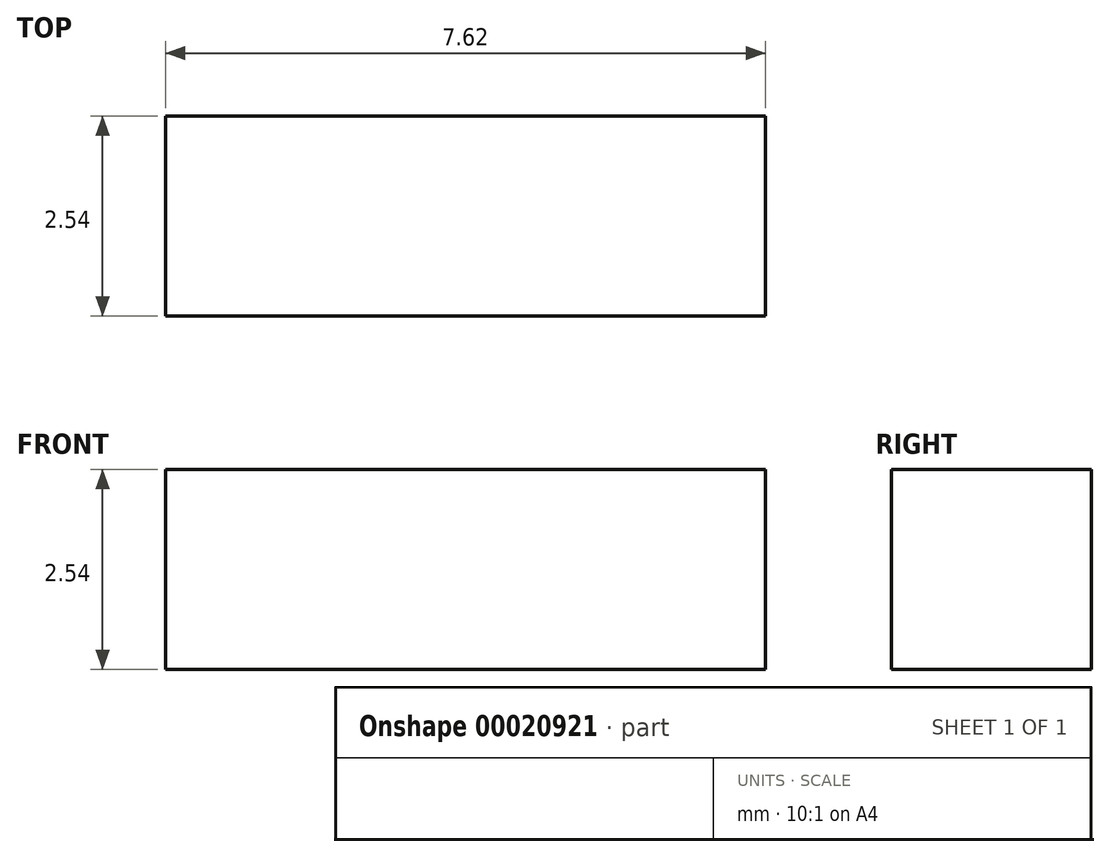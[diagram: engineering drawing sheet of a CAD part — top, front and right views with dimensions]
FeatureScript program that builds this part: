
annotation { "Feature Type Name" : "Feature", "Feature Type Description" : "" }
export const myFeature = defineFeature(function(context is Context, id is Id, definition is map)
    precondition{}
    {
        {
            var Q0;
            Q0=qCreatedBy(makeId("Front.planeOp"),FACE);
            var sketch = newSketch(context, id + "F0", { "sketchPlane" : qUnion([Q0])});
            skLineSegment(sketch, "E0.rect.bottom", {"start": v(3.81, 1.27) * mm, "end": v(-3.8, 1.27) * mm});
            skLineSegment(sketch, "E0.rect.top", {"start": v(3.81, -1.27) * mm, "end": v(-3.81, -1.27) * mm});
            skLineSegment(sketch, "E0.rect.left", {"start": v(3.81, 1.27) * mm, "end": v(3.81, -1.27) * mm});
            skLineSegment(sketch, "E0.rect.right", {"start": v(-3.81, 1.27) * mm, "end": v(-3.81, -1.27) * mm});
            skPoint(sketch, "E0.rect.middle", {"position": v(0, 0) * mm});
            skSolve(sketch);
        }
        {
            var Q0;
            Q0 = qSketchRegion(id + "F0", true);
            extrude(context, id + "F1", {"entities" : qUnion([Q0]), "depth" : 2.54 * mm});
        }
    });
